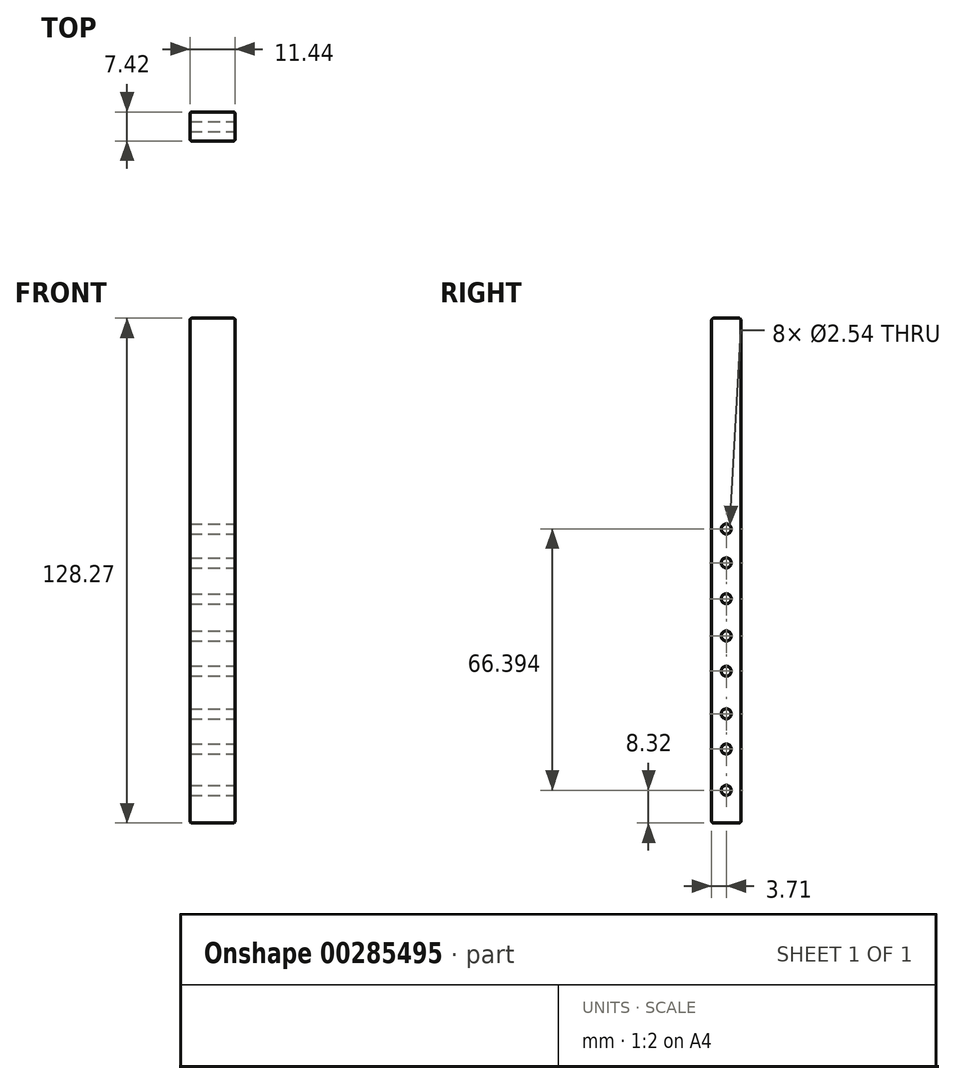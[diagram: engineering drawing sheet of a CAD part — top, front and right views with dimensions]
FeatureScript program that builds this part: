
annotation { "Feature Type Name" : "Feature", "Feature Type Description" : "" }
export const myFeature = defineFeature(function(context is Context, id is Id, definition is map)
    precondition{}
    {
        {
            var Q0;
            Q0=qCreatedBy(makeId("Top.planeOp"),FACE);
            var sketch = newSketch(context, id + "F0", { "sketchPlane" : qUnion([Q0])});
            skLineSegment(sketch, "E0.bottom", {"start": v(5.72, -3.71) * mm, "end": v(-5.72, -3.71) * mm});
            skLineSegment(sketch, "E0.top", {"start": v(5.72, 3.71) * mm, "end": v(-5.72, 3.71) * mm});
            skLineSegment(sketch, "E0.left", {"start": v(5.72, -3.71) * mm, "end": v(5.72, 3.71) * mm});
            skLineSegment(sketch, "E0.right", {"start": v(-5.72, -3.71) * mm, "end": v(-5.72, 3.71) * mm});
            skPoint(sketch, "E0.middle", {"position": v(0, 0) * mm});
            skSolve(sketch);
        }
        {
            var Q0;
            Q0=makeQuery(id+"F0.imprint","IMPRINT",FACE,{"disambiguationData":[TD([[makeQuery(id+"F0.imprint","IMPRINT",EDGE,{"derivedFrom":sQuery(id+"F0.wireOp",EDGE,"E0.bottom")}),-1.0]])]});
            extrude(context, id + "F1", {"entities" : qUnion([Q0]), "depth" : 128.27 * mm});
        }
        {
            var Q0;
            Q0=makeQuery(id+"F1.opExtrude","SWEPT_FACE",FACE,{"disambiguationData":[OSD([sQuery(id+"F0.wireOp",EDGE,"E0.right")])]});
            var Q1;
            Q1=makeQuery(id+"F1.opExtrude","SWEPT_FACE",FACE,{"disambiguationData":[OSD([sQuery(id+"F0.wireOp",EDGE,"E0.bottom")])]});
            var Q2;
            Q2=makeQuery(id+"F1.opExtrude","CAP_FACE",FACE,{"disambiguationData":[OSD([sQuery(id+"F0.wireOp",EDGE,"E0.bottom"),sQuery(id+"F0.wireOp",EDGE,"E0.top"),sQuery(id+"F0.wireOp",EDGE,"E0.left"),sQuery(id+"F0.wireOp",EDGE,"E0.right")])],"isStart":false});
            var Q3;
            Q3=makeQuery(id+"F1.opExtrude","SWEPT_FACE",FACE,{"disambiguationData":[OSD([sQuery(id+"F0.wireOp",EDGE,"E0.left")])]});
            var Q4;
            Q4=makeQuery(id+"F1.opExtrude","SWEPT_FACE",FACE,{"disambiguationData":[OSD([sQuery(id+"F0.wireOp",EDGE,"E0.top")])]});
            fillet(context, id + "F2", {"entities" : qUnion([Q0, Q1, Q2, Q3, Q4]), "radius" : 0.5 * mm, "tangentPropagation" : true, "allowEdgeOverflow" : false});
        }
        {
            var Q0;
            Q0=qCreatedBy(makeId("Right.planeOp"),FACE);
            var sketch = newSketch(context, id + "F3", { "sketchPlane" : qUnion([Q0])});
            skLineSegment(sketch, "E1", {"start": v(0, 74.71) * mm, "end": v(0, 66.11) * mm});
            skLineSegment(sketch, "E2", {"start": v(0, 66.11) * mm, "end": v(0, 57) * mm});
            skLineSegment(sketch, "E3", {"start": v(0, 57) * mm, "end": v(0, 47.54) * mm});
            skLineSegment(sketch, "E4", {"start": v(0, 47.54) * mm, "end": v(0, 38.6) * mm});
            skLineSegment(sketch, "E5", {"start": v(0, 38.6) * mm, "end": v(0, 27.76) * mm});
            skLineSegment(sketch, "E6", {"start": v(0, 27.76) * mm, "end": v(0, 18.81) * mm});
            skLineSegment(sketch, "E7", {"start": v(0, 18.81) * mm, "end": v(0, 8.32) * mm});
            skSolve(sketch);
        }
        {
            var Q0;
            Q0=sQuery(id+"F3.wireOp",VERTEX,"E1.start");
            var Q1;
            Q1=sQuery(id+"F3.wireOp",VERTEX,"E2.start");
            var Q2;
            Q2=sQuery(id+"F3.wireOp",VERTEX,"E3.start");
            var Q3;
            Q3=sQuery(id+"F3.wireOp",VERTEX,"E4.start");
            var Q4;
            Q4=sQuery(id+"F3.wireOp",VERTEX,"E5.start");
            var Q5;
            Q5=sQuery(id+"F3.wireOp",VERTEX,"E6.start");
            var Q6;
            Q6=sQuery(id+"F3.wireOp",VERTEX,"E7.start");
            var Q7;
            Q7=sQuery(id+"F3.wireOp",VERTEX,"E7.end");
            var Q8;
            Q8=makeQuery(id+"F1.opExtrude","SWEPT_BODY",BODY,{"disambiguationData":[OSD([sQuery(id+"F0.wireOp",EDGE,"E0.bottom"),sQuery(id+"F0.wireOp",EDGE,"E0.top"),sQuery(id+"F0.wireOp",EDGE,"E0.left"),sQuery(id+"F0.wireOp",EDGE,"E0.right")])]});
            hole(context, id + "F4", {"style" : HoleStyle.SIMPLE, "endStyle" : HoleEndStyle.BLIND, "holeDiameter" : 2.54 * mm, "holeDepth" : 12.7 * mm, "tappedDepth" : 12.7 * mm, "tapClearance" : 3, "locations" : qUnion([Q0, Q1, Q2, Q3, Q4, Q5, Q6, Q7]), "scope" : qUnion([Q8])});
        }
        {
            var Q0;
            Q0=sQuery(id+"F3.wireOp",VERTEX,"E1.start");
            var Q1;
            Q1=sQuery(id+"F3.wireOp",VERTEX,"E2.start");
            var Q2;
            Q2=sQuery(id+"F3.wireOp",VERTEX,"E3.start");
            var Q3;
            Q3=sQuery(id+"F3.wireOp",VERTEX,"E4.start");
            var Q4;
            Q4=sQuery(id+"F3.wireOp",VERTEX,"E5.start");
            var Q5;
            Q5=sQuery(id+"F3.wireOp",VERTEX,"E6.start");
            var Q6;
            Q6=sQuery(id+"F3.wireOp",VERTEX,"E7.start");
            var Q7;
            Q7=sQuery(id+"F3.wireOp",VERTEX,"E7.end");
            var Q8;
            Q8=makeQuery(id+"F1.opExtrude","SWEPT_BODY",BODY,{"disambiguationData":[OSD([sQuery(id+"F0.wireOp",EDGE,"E0.bottom"),sQuery(id+"F0.wireOp",EDGE,"E0.top"),sQuery(id+"F0.wireOp",EDGE,"E0.left"),sQuery(id+"F0.wireOp",EDGE,"E0.right")])]});
            hole(context, id + "F5", {"style" : HoleStyle.SIMPLE, "endStyle" : HoleEndStyle.BLIND, "oppositeDirection" : true, "holeDiameter" : 2.54 * mm, "holeDepth" : 12.7 * mm, "tappedDepth" : 12.7 * mm, "tapClearance" : 3, "locations" : qUnion([Q0, Q1, Q2, Q3, Q4, Q5, Q6, Q7]), "scope" : qUnion([Q8])});
        }
    });
